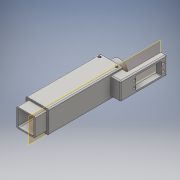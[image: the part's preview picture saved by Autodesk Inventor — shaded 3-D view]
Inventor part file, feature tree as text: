
AUTODESK INVENTOR PART (.ipt)
format: ipt  version: 2016 (Build 200138000, 138)  size: 341,504 bytes
history: native  units: mm
features: extrude x17, sketch x14, fillet x4, other x2
ambient origin geometry x8: Origin, YZ Plane, XZ Plane, XY Plane, X Axis, Y Axis, Z Axis, Center Point
bodies: Body1 (feature_tree)
feature tree (37):
  other  "ソリッド1"
  extrude  "押し出し1"  Depth=33.0mm
  fillet  "フィレット1"  Radius=33.0mm
  extrude  "押し出し2"  Depth=20.0mm TaperAngle=0.0deg
  fillet  "フィレット2"  Radius=2.0mm
  extrude  "押し出し3"  Depth=3.5mm
  extrude  "押し出し5"  Depth=3.5mm
  extrude  "押し出し6"  Depth=3.5mm
  extrude  "押し出し7"  Depth=3.5mm
  extrude  "押し出し8"  Depth=30.0mm TaperAngle=0.0deg
  extrude  "押し出し9"  Depth=2.0mm
  extrude  "押し出し10"  Depth=2.0mm
  extrude  "押し出し11"  Depth=2.5mm
  fillet  "フィレット3"  Radius=2.5mm
  sketch  "スケッチ11"
  extrude  "押し出し12"  Depth=2.5mm
  extrude  "押し出し13"  Depth=2.5mm
  extrude  "押し出し14"  Depth=30.0mm TaperAngle=0.0deg
  extrude  "押し出し15"  Depth=2.0mm
  extrude  "押し出し25"  Depth=3.0mm
  other  "作業平面1"
  extrude  "押し出し29"  Depth=3.0mm
  extrude  "押し出し30"  Depth=3.0mm
  fillet  "フィレット6"  Radius=3.0mm
  sketch  "スケッチ1"
  sketch  "スケッチ2"
  sketch  "スケッチ3"
  sketch  "スケッチ4"
  sketch  "スケッチ5"
  sketch  "スケッチ6"
  sketch  "スケッチ7"
  sketch  "スケッチ8"
  sketch  "スケッチ9"
  sketch  "スケッチ10"
  sketch  "スケッチ21"
  sketch  "スケッチ24"
  sketch  "スケッチ25"
